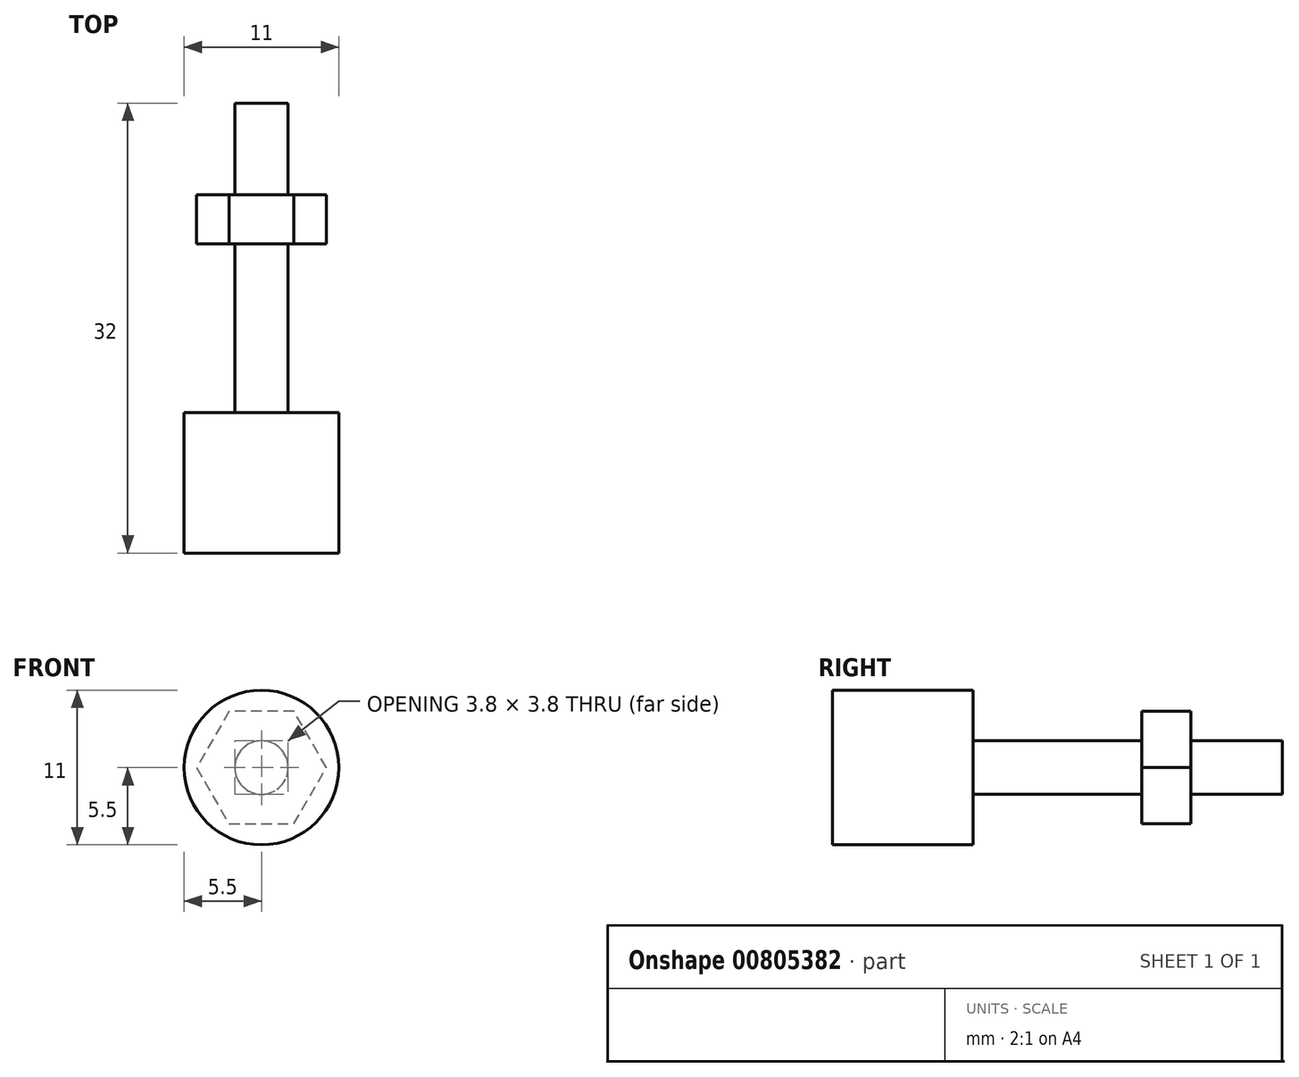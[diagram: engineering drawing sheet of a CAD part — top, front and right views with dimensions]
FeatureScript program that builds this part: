
annotation { "Feature Type Name" : "Feature", "Feature Type Description" : "" }
export const myFeature = defineFeature(function(context is Context, id is Id, definition is map)
    precondition{}
    {
        {
            var Q0;
            Q0=qCreatedBy(makeId("Front.planeOp"),FACE);
            var sketch = newSketch(context, id + "F0", { "sketchPlane" : qUnion([Q0])});
            skCircle(sketch, "E0", {"center": v(0, 0) * mm, "radius": 5.5 * mm});
            skCircle(sketch, "E1", {"center": v(0, 0) * mm, "radius": 1.9 * mm});
            skSolve(sketch);
        }
        {
            var Q0;
            Q0 = qSketchRegion(id + "F0", true);
            var Q1;
            Q1=makeQuery(id+"F0.imprint","IMPRINT",FACE,{"disambiguationData":[TD([[makeQuery(id+"F0.imprint","IMPRINT",EDGE,{"derivedFrom":sQuery(id+"F0.wireOp",EDGE,"E1")}),1.0]])]});
            extrude(context, id + "F1", {"entities" : qUnion([Q0, Q1]), "depth" : 10 * mm, "offsetDistance" : 25 * mm, "hasDraft" : true, "draftAngle" : 0 * degree});
        }
        {
            var Q0;
            Q0=makeQuery(id+"F0.imprint","IMPRINT",FACE,{"disambiguationData":[TD([[makeQuery(id+"F0.imprint","IMPRINT",EDGE,{"derivedFrom":sQuery(id+"F0.wireOp",EDGE,"E1")}),1.0]])]});
            extrude(context, id + "F2", {"entities" : qUnion([Q0]), "operationType" : NewBodyOperationType.ADD, "oppositeDirection" : true, "depth" : 22 * mm, "offsetDistance" : 25 * mm});
        }
        {
            var Q0;
            Q0=makeQuery(id+"F2.opExtrude","CAP_FACE",FACE,{"disambiguationData":[OSD([sQuery(id+"F0.wireOp",EDGE,"E1")])],"isStart":false});
            var sketch = newSketch(context, id + "F3", { "sketchPlane" : qUnion([Q0])});
            skCircle(sketch, "E2.cCircle", {"center": v(0, 0) * mm, "radius": 4 * mm, "construction": true});
            skLineSegment(sketch, "E2.0", {"start": v(-2.3, 4) * mm, "end": v(2.3, 4) * mm});
            skLineSegment(sketch, "E2.1", {"start": v(2.3, 4) * mm, "end": v(4.62, 0) * mm});
            skLineSegment(sketch, "E2.2", {"start": v(4.62, 0) * mm, "end": v(2.3, -4) * mm});
            skLineSegment(sketch, "E2.3", {"start": v(2.3, -4) * mm, "end": v(-2.3, -4) * mm});
            skLineSegment(sketch, "E2.4", {"start": v(-2.3, -4) * mm, "end": v(-4.62, 0) * mm});
            skLineSegment(sketch, "E2.5", {"start": v(-4.62, 0) * mm, "end": v(-2.3, 4) * mm});
            skPoint(sketch, "E2.0.midPoint", {"position": v(0, 4) * mm});
            skSolve(sketch);
        }
        {
            var Q0;
            Q0 = qSketchRegion(id + "F3", true);
            extrude(context, id + "F4", {"entities" : qUnion([Q0]), "operationType" : NewBodyOperationType.ADD, "oppositeDirection" : true, "depth" : 10 * mm, "offsetDistance" : 25 * mm, "hasSecondDirection" : true, "secondDirectionOppositeDirection" : true, "secondDirectionDepth" : 6.5 * mm});
        }
    });
